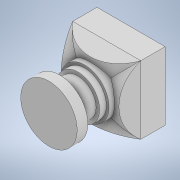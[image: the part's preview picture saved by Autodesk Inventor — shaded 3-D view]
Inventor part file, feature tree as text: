
AUTODESK INVENTOR PART (.ipt)
format: ipt  version: 2020 (Build 240168000, 168)  size: 232,448 bytes
history: native  units: in
note: dims shown in document units (in); Inventor stores cm internally (conversion verified against a paired STEP export)
features: sketch x11, extrude x9, projected_geometry x8, plane x2
ambient origin geometry x8: Origin, YZ Plane, XZ Plane, XY Plane, X Axis, Y Axis, Z Axis, Center Point
bodies: Solid1 (feature_tree)
feature tree (30):
  extrude  "Extrusion1"  Depth=0.8819in
  extrude  "Extrusion2"  Depth=0.6299in
  sketch  "Sketch3"  dims[d5=0.2854in d6=0.0in d9=0.2165in]
  extrude  "Extrusion4"  Depth=0.2165in
  extrude  "Extrusion5"  Depth=0.0886in
  extrude  "Extrusion6"  Depth=0.374in
  extrude  "Extrusion7"  Depth=0.374in
  extrude  "Extrusion8"  Depth=0.0886in TaperAngle=0.0deg
  extrude  "Extrusion9"  Depth=0.2362in TaperAngle=0.0deg
  extrude  "Extrusion10"  Depth=0.1378in TaperAngle=0.0deg
  sketch  "Sketch12"  dims[d36=0.0394in d41=0.4409in]
  plane  "Work Plane2"
  plane  "Work Plane3"
  sketch  "Sketch1"  dims[d0=0.8819in d1=0.8819in]
  sketch  "Sketch2"  dims[d2=0.315in d3=0.0in d4=0.6299in]
  projected_geometry  "Projected Loop1"
  sketch  "Sketch5"  dims[d10=0.0886in d11=0.0in d12=0.2165in]
  projected_geometry  "Projected Loop3"
  sketch  "Sketch6"  dims[d13=0.0886in d14=0.0in d15=0.374in]
  projected_geometry  "Projected Loop4"
  sketch  "Sketch7"  dims[d16=0.0886in d17=0.0in d18=0.374in]
  projected_geometry  "Projected Loop5"
  sketch  "Sketch8"  dims[d19=0.0886in d20=0.0in d23=0.0886in d24=0.0in]
  projected_geometry  "Projected Loop6"
  projected_geometry  "Projected Loop7"
  sketch  "Sketch9"  dims[d25=0.0787in d26=0.2362in d27=0.0in]
  projected_geometry  "Projected Loop8"
  sketch  "Sketch10"  dims[d28=0.7307in d29=0.1378in d30=0.0in]
  projected_geometry  "Projected Loop9"
  sketch  "Sketch11"  dims[d31=1.063in]
